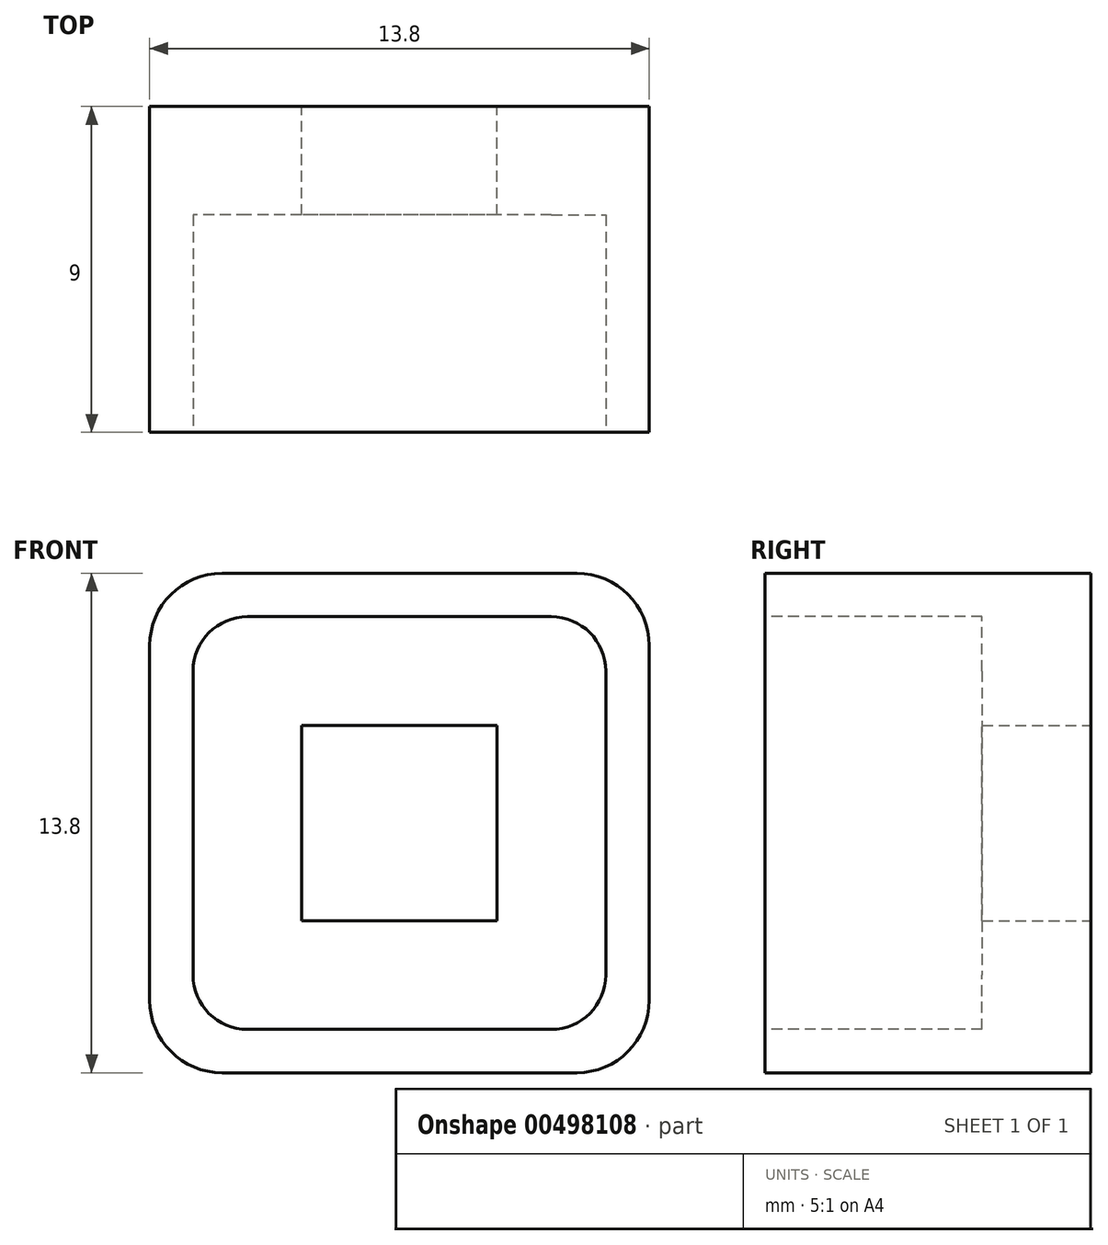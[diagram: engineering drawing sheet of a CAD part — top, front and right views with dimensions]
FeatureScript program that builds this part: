
annotation { "Feature Type Name" : "Feature", "Feature Type Description" : "" }
export const myFeature = defineFeature(function(context is Context, id is Id, definition is map)
    precondition{}
    {
        {
            var Q0;
            Q0=qCreatedBy(makeId("Front.planeOp"),FACE);
            var sketch = newSketch(context, id + "F0", { "sketchPlane" : qUnion([Q0])});
            skLineSegment(sketch, "E0.bottom", {"start": v(6.9, 6.9) * mm, "end": v(-6.9, 6.9) * mm});
            skLineSegment(sketch, "E0.top", {"start": v(6.9, -6.9) * mm, "end": v(-6.9, -6.9) * mm});
            skLineSegment(sketch, "E0.left", {"start": v(6.9, 6.9) * mm, "end": v(6.9, -6.9) * mm});
            skLineSegment(sketch, "E0.right", {"start": v(-6.9, 6.9) * mm, "end": v(-6.9, -6.9) * mm});
            skPoint(sketch, "E0.middle", {"position": v(0, 0) * mm});
            skSolve(sketch);
        }
        {
            var Q0;
            Q0 = qSketchRegion(id + "F0", true);
            extrude(context, id + "F1", {"entities" : qUnion([Q0]), "depth" : 9 * mm});
        }
        {
            var Q0;
            Q0=qCreatedBy(makeId("Front.planeOp"),FACE);
            var sketch = newSketch(context, id + "F2", { "sketchPlane" : qUnion([Q0])});
            skLineSegment(sketch, "E1.bottom", {"start": v(-2.7, 2.7) * mm, "end": v(2.7, 2.7) * mm});
            skLineSegment(sketch, "E1.top", {"start": v(-2.7, -2.7) * mm, "end": v(2.7, -2.7) * mm});
            skLineSegment(sketch, "E1.left", {"start": v(-2.7, 2.7) * mm, "end": v(-2.7, -2.7) * mm});
            skLineSegment(sketch, "E1.right", {"start": v(2.7, 2.7) * mm, "end": v(2.7, -2.7) * mm});
            skPoint(sketch, "E1.middle", {"position": v(0, 0) * mm});
            skSolve(sketch);
        }
        {
            var Q0;
            Q0=makeQuery(id+"F2.imprint","IMPRINT",FACE,{"disambiguationData":[TD([[makeQuery(id+"F2.imprint","IMPRINT",EDGE,{"derivedFrom":sQuery(id+"F2.wireOp",EDGE,"E1.bottom")}),-1.0]])]});
            extrude(context, id + "F3", {"entities" : qUnion([Q0]), "operationType" : NewBodyOperationType.REMOVE, "endBound" : BoundingType.THROUGH_ALL, "depth" : 3 * mm});
        }
        {
            var Q0;
            Q0=makeQuery(id+"F1.opExtrude","CAP_FACE",FACE,{"disambiguationData":[OSD([sQuery(id+"F0.wireOp",EDGE,"E0.bottom"),sQuery(id+"F0.wireOp",EDGE,"E0.top"),sQuery(id+"F0.wireOp",EDGE,"E0.left"),sQuery(id+"F0.wireOp",EDGE,"E0.right")])],"isStart":false});
            var sketch = newSketch(context, id + "F4", { "sketchPlane" : qUnion([Q0])});
            skLineSegment(sketch, "E2.bottom", {"start": v(5.7, 5.7) * mm, "end": v(-5.7, 5.7) * mm});
            skLineSegment(sketch, "E2.top", {"start": v(5.7, -5.7) * mm, "end": v(-5.7, -5.7) * mm});
            skLineSegment(sketch, "E2.left", {"start": v(5.7, 5.7) * mm, "end": v(5.7, -5.7) * mm});
            skLineSegment(sketch, "E2.right", {"start": v(-5.7, 5.7) * mm, "end": v(-5.7, -5.7) * mm});
            skPoint(sketch, "E2.middle", {"position": v(0, 0) * mm});
            skSolve(sketch);
        }
        {
            var Q0;
            Q0=makeQuery(id+"F4.imprint","IMPRINT",FACE,{"disambiguationData":[TD([[makeQuery(id+"F4.imprint","IMPRINT",EDGE,{"derivedFrom":sQuery(id+"F4.wireOp",EDGE,"E2.bottom")}),1.0]])]});
            extrude(context, id + "F5", {"entities" : qUnion([Q0]), "operationType" : NewBodyOperationType.REMOVE, "oppositeDirection" : true, "depth" : 6 * mm});
        }
        {
            var Q0;
            Q0=makeQuery(id+"F1.opExtrude","SWEPT_EDGE",EDGE,{"disambiguationData":[OSD([sQuery(id+"F0.wireOp",EDGE,"E0.bottom"),sQuery(id+"F0.wireOp",EDGE,"E0.right")])]});
            var Q1;
            Q1=makeQuery(id+"F1.opExtrude","SWEPT_EDGE",EDGE,{"disambiguationData":[OSD([sQuery(id+"F0.wireOp",EDGE,"E0.top"),sQuery(id+"F0.wireOp",EDGE,"E0.right")])]});
            var Q2;
            Q2=makeQuery(id+"F1.opExtrude","SWEPT_EDGE",EDGE,{"disambiguationData":[OSD([sQuery(id+"F0.wireOp",EDGE,"E0.bottom"),sQuery(id+"F0.wireOp",EDGE,"E0.left")])]});
            var Q3;
            Q3=makeQuery(id+"F1.opExtrude","SWEPT_EDGE",EDGE,{"disambiguationData":[OSD([sQuery(id+"F0.wireOp",EDGE,"E0.top"),sQuery(id+"F0.wireOp",EDGE,"E0.left")])]});
            fillet(context, id + "F6", {"entities" : qUnion([Q0, Q1, Q2, Q3]), "radius" : 2 * mm, "tangentPropagation" : true, "allowEdgeOverflow" : false});
        }
        {
            var Q0;
            Q0=makeQuery(id+"F5.boolean.opBoolean","COPY",EDGE,{"derivedFrom":makeQuery(id+"F5.opExtrude","SWEPT_EDGE",EDGE,{"disambiguationData":[OSD([sQuery(id+"F4.wireOp",EDGE,"E2.bottom"),sQuery(id+"F4.wireOp",EDGE,"E2.right")])]})});
            var Q1;
            Q1=makeQuery(id+"F5.boolean.opBoolean","COPY",EDGE,{"derivedFrom":makeQuery(id+"F5.opExtrude","SWEPT_EDGE",EDGE,{"disambiguationData":[OSD([sQuery(id+"F4.wireOp",EDGE,"E2.bottom"),sQuery(id+"F4.wireOp",EDGE,"E2.left")])]})});
            var Q2;
            Q2=makeQuery(id+"F5.boolean.opBoolean","COPY",EDGE,{"derivedFrom":makeQuery(id+"F5.opExtrude","SWEPT_EDGE",EDGE,{"disambiguationData":[OSD([sQuery(id+"F4.wireOp",EDGE,"E2.top"),sQuery(id+"F4.wireOp",EDGE,"E2.right")])]})});
            var Q3;
            Q3=makeQuery(id+"F5.boolean.opBoolean","COPY",EDGE,{"derivedFrom":makeQuery(id+"F5.opExtrude","SWEPT_EDGE",EDGE,{"disambiguationData":[OSD([sQuery(id+"F4.wireOp",EDGE,"E2.top"),sQuery(id+"F4.wireOp",EDGE,"E2.left")])]})});
            fillet(context, id + "F7", {"entities" : qUnion([Q0, Q1, Q2, Q3]), "radius" : 1.5 * mm, "tangentPropagation" : true, "allowEdgeOverflow" : false});
        }
    });
